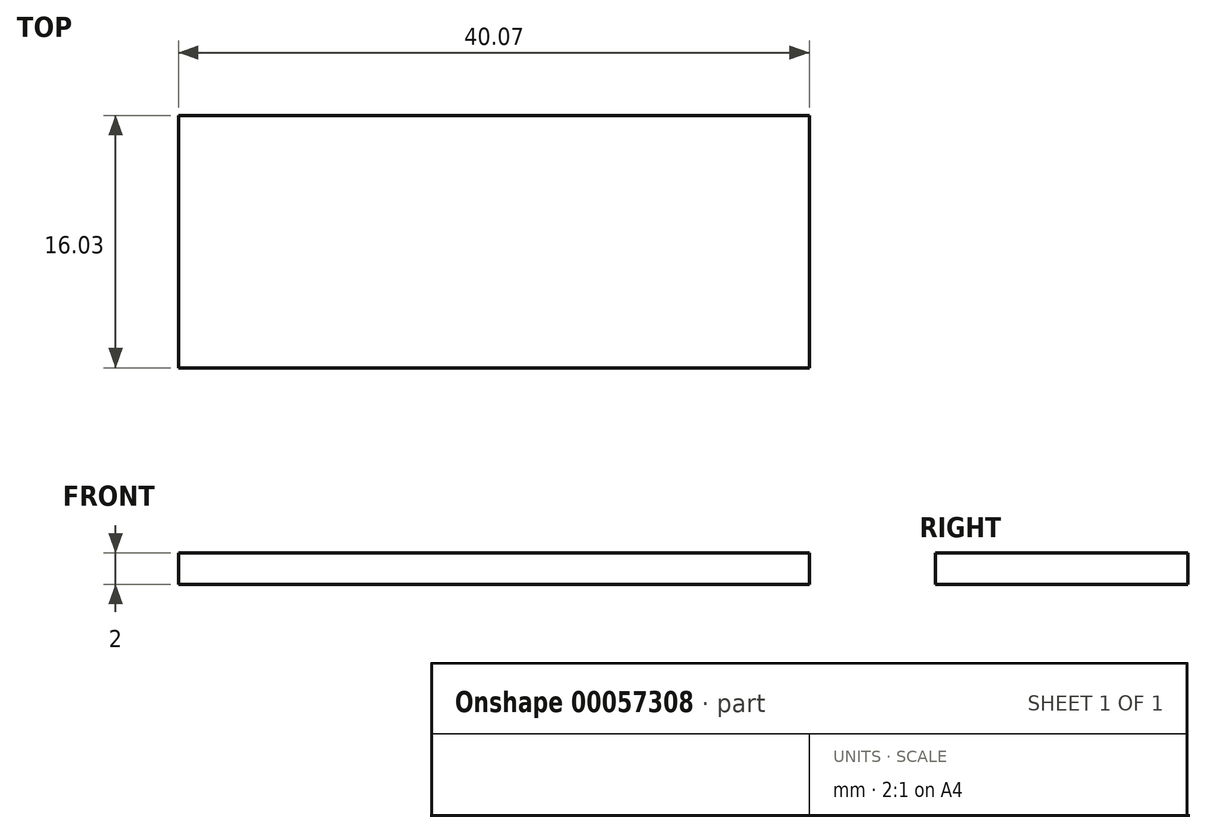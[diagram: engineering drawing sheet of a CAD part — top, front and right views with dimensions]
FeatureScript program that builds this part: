
annotation { "Feature Type Name" : "Feature", "Feature Type Description" : "" }
export const myFeature = defineFeature(function(context is Context, id is Id, definition is map)
    precondition{}
    {
        {
            var Q0;
            Q0=qCreatedBy(makeId("Top.planeOp"),FACE);
            var sketch = newSketch(context, id + "F0", { "sketchPlane" : qUnion([Q0])});
            skLineSegment(sketch, "E0.bottom", {"start": v(-20.57, 30.32) * mm, "end": v(19.5, 30.32) * mm});
            skLineSegment(sketch, "E0.top", {"start": v(-20.57, 14.3) * mm, "end": v(19.5, 14.3) * mm});
            skLineSegment(sketch, "E0.left", {"start": v(-20.57, 30.32) * mm, "end": v(-20.57, 14.3) * mm});
            skLineSegment(sketch, "E0.right", {"start": v(19.5, 30.32) * mm, "end": v(19.5, 14.3) * mm});
            skSolve(sketch);
        }
        {
            var Q0;
            Q0 = qSketchRegion(id + "F0", true);
            extrude(context, id + "F1", {"entities" : qUnion([Q0]), "depth" : 2 * mm});
        }
    });
